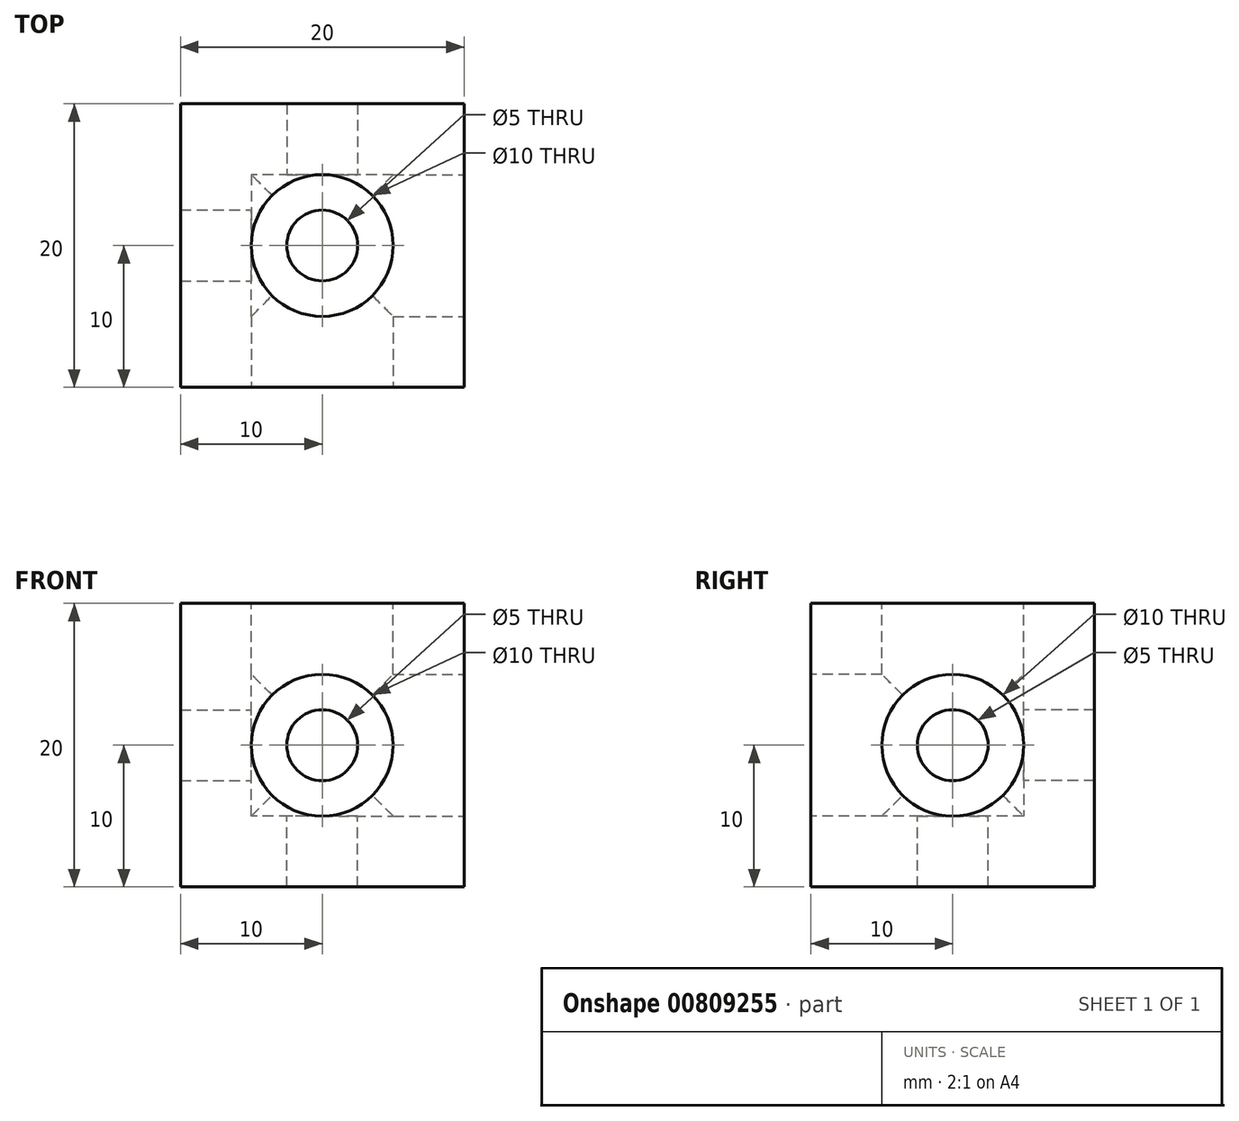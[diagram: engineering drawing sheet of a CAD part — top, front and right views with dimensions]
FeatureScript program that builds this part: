
annotation { "Feature Type Name" : "Feature", "Feature Type Description" : "" }
export const myFeature = defineFeature(function(context is Context, id is Id, definition is map)
    precondition{}
    {
        {
            var Q0;
            Q0=qCreatedBy(makeId("Top.planeOp"),FACE);
            var sketch = newSketch(context, id + "F0", { "sketchPlane" : qUnion([Q0])});
            skLineSegment(sketch, "E0.bottom", {"start": v(10, -10) * mm, "end": v(-10, -10) * mm});
            skLineSegment(sketch, "E0.top", {"start": v(10, 10) * mm, "end": v(-10, 10) * mm});
            skLineSegment(sketch, "E0.left", {"start": v(10, -10) * mm, "end": v(10, 10) * mm});
            skLineSegment(sketch, "E0.right", {"start": v(-10, -10) * mm, "end": v(-10, 10) * mm});
            skPoint(sketch, "E0.middle", {"position": v(0, 0) * mm});
            skSolve(sketch);
        }
        {
            var Q0;
            Q0 = qSketchRegion(id + "F0", true);
            extrude(context, id + "F1", {"entities" : qUnion([Q0]), "depth" : 20 * mm, "offsetDistance" : 25 * mm});
        }
        {
            var Q0;
            Q0=makeQuery(id+"F1.opExtrude","SWEPT_FACE",FACE,{"disambiguationData":[OSD([sQuery(id+"F0.wireOp",EDGE,"E0.bottom")])]});
            var sketch = newSketch(context, id + "F2", { "sketchPlane" : qUnion([Q0])});
            skPoint(sketch, "E1", {"position": v(0, 10) * mm});
            skPoint(sketch, "E1.positionSnap0", {"position": v(10, 10) * mm});
            skSolve(sketch);
        }
        {
            var Q0;
            Q0=makeQuery(id+"F1.opExtrude","SWEPT_FACE",FACE,{"disambiguationData":[OSD([sQuery(id+"F0.wireOp",EDGE,"E0.left")])]});
            var sketch = newSketch(context, id + "F3", { "sketchPlane" : qUnion([Q0])});
            skPoint(sketch, "E2", {"position": v(0, 10) * mm});
            skPoint(sketch, "E2.positionSnap0", {"position": v(-10, 10) * mm});
            skSolve(sketch);
        }
        {
            var Q0;
            Q0=makeQuery(id+"F1.opExtrude","CAP_FACE",FACE,{"disambiguationData":[OSD([sQuery(id+"F0.wireOp",EDGE,"E0.bottom"),sQuery(id+"F0.wireOp",EDGE,"E0.top"),sQuery(id+"F0.wireOp",EDGE,"E0.left"),sQuery(id+"F0.wireOp",EDGE,"E0.right")])],"isStart":false});
            var sketch = newSketch(context, id + "F4", { "sketchPlane" : qUnion([Q0])});
            skPoint(sketch, "E3", {"position": v(0, 0) * mm});
            skSolve(sketch);
        }
        {
            var Q0;
            Q0=sQuery(id+"F2.wireOp",VERTEX,"E1");
            var Q1;
            Q1=sQuery(id+"F3.wireOp",VERTEX,"E2");
            var Q2;
            Q2=sQuery(id+"F4.wireOp",VERTEX,"E3");
            var Q3;
            Q3=makeQuery(id+"F1.opExtrude","SWEPT_BODY",BODY,{"disambiguationData":[OSD([sQuery(id+"F0.wireOp",EDGE,"E0.bottom"),sQuery(id+"F0.wireOp",EDGE,"E0.top"),sQuery(id+"F0.wireOp",EDGE,"E0.left"),sQuery(id+"F0.wireOp",EDGE,"E0.right")])]});
            hole(context, id + "F5", {"style" : HoleStyle.C_BORE, "endStyle" : HoleEndStyle.THROUGH, "holeDiameter" : 5 * mm, "cBoreDiameter" : 10 * mm, "cBoreDepth" : 15 * mm, "majorDiameter" : 5 * mm, "isTappedThrough" : true, "tappedDepth" : 12 * mm, "tapClearance" : 3, "locations" : qUnion([Q0, Q1, Q2]), "scope" : qUnion([Q3])});
        }
    });
